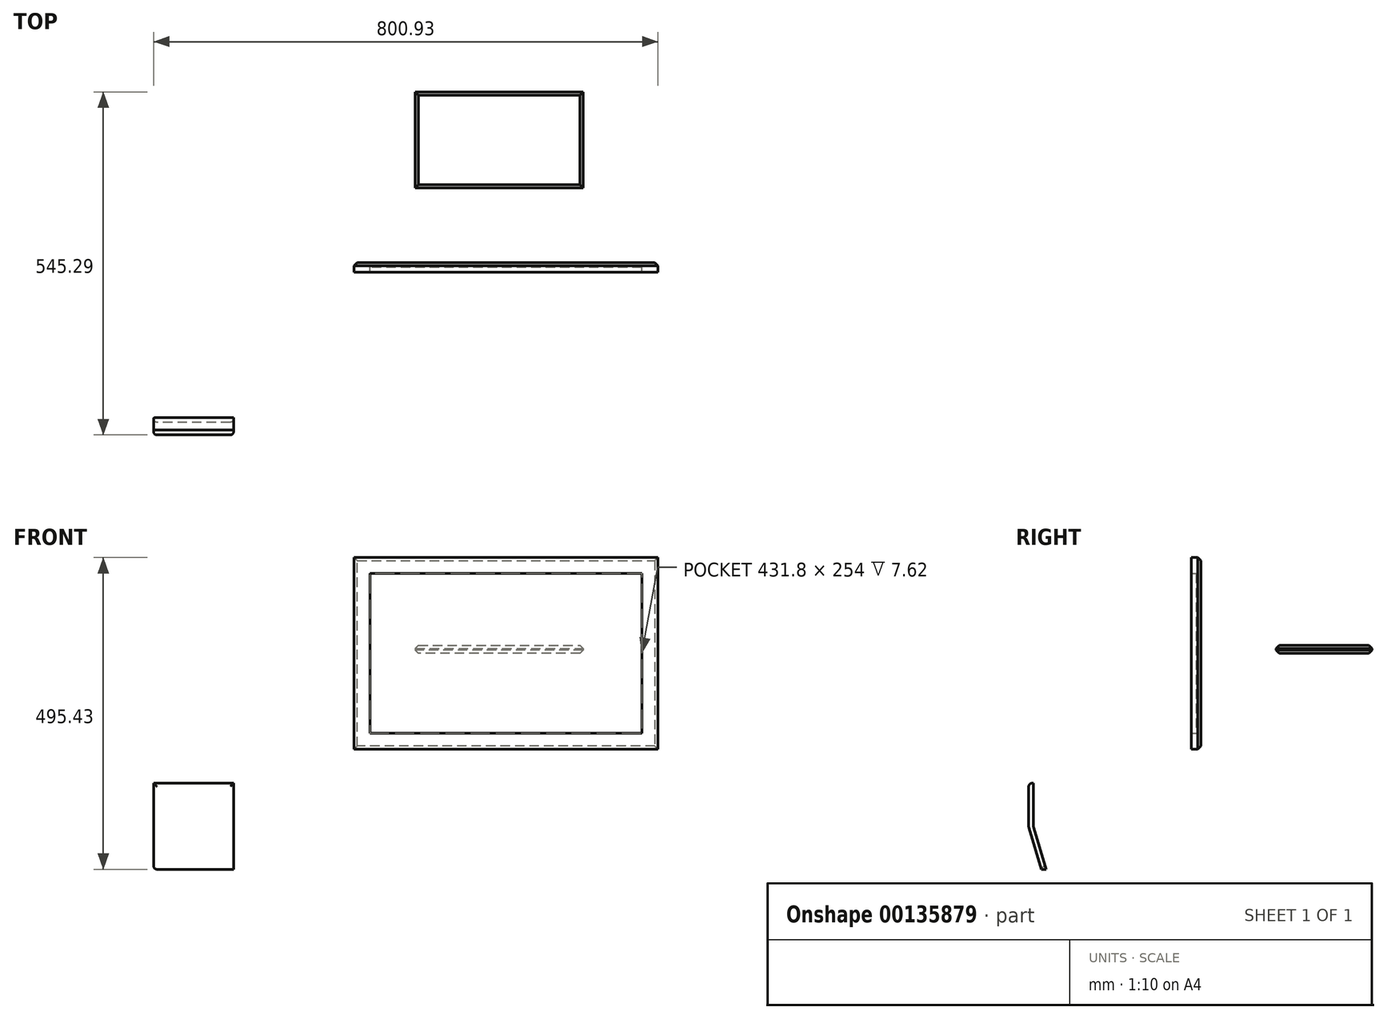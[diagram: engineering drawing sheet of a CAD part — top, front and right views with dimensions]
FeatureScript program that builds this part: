
annotation { "Feature Type Name" : "Feature", "Feature Type Description" : "" }
export const myFeature = defineFeature(function(context is Context, id is Id, definition is map)
    precondition{}
    {
        {
            var Q0;
            Q0=qCreatedBy(makeId("Front.planeOp"),FACE);
            var sketch = newSketch(context, id + "F0", { "sketchPlane" : qUnion([Q0])});
            skLineSegment(sketch, "E0.bottom", {"start": v(775.53, 127) * mm, "end": v(343.73, 127) * mm});
            skLineSegment(sketch, "E0.top", {"start": v(775.53, -127) * mm, "end": v(343.73, -127) * mm});
            skLineSegment(sketch, "E0.left", {"start": v(775.53, 127) * mm, "end": v(775.53, -127) * mm});
            skLineSegment(sketch, "E0.right", {"start": v(343.73, 127) * mm, "end": v(343.73, -127) * mm});
            skPoint(sketch, "E0.middle", {"position": v(559.63, 0) * mm});
            skLineSegment(sketch, "E1.bottom", {"start": v(800.93, -152.4) * mm, "end": v(318.33, -152.4) * mm});
            skLineSegment(sketch, "E1.top", {"start": v(800.93, 152.4) * mm, "end": v(318.33, 152.4) * mm});
            skLineSegment(sketch, "E1.left", {"start": v(800.93, -152.4) * mm, "end": v(800.93, 152.4) * mm});
            skLineSegment(sketch, "E1.right", {"start": v(318.33, -152.4) * mm, "end": v(318.33, 152.4) * mm});
            skPoint(sketch, "E2.middle", {"position": v(559.63, -218.6) * mm});
            skPoint(sketch, "E2.middle.positionSnap0", {"position": v(559.63, -152.4) * mm});
            skSolve(sketch);
        }
        {
            var Q0;
            Q0=makeQuery(id+"F0.imprint","IMPRINT",FACE,{"disambiguationData":[TD([[makeQuery(id+"F0.imprint","IMPRINT",EDGE,{"derivedFrom":sQuery(id+"F0.wireOp",EDGE,"E0.bottom")}),-1.0]])]});
            extrude(context, id + "F1", {"entities" : qUnion([Q0]), "depth" : 15.24 * mm});
        }
        {
            var Q0;
            Q0=makeQuery(id+"F0.imprint","IMPRINT",FACE,{"disambiguationData":[TD([[makeQuery(id+"F0.imprint","IMPRINT",EDGE,{"derivedFrom":sQuery(id+"F0.wireOp",EDGE,"E0.bottom")}),1.0]])]});
            extrude(context, id + "F2", {"entities" : qUnion([Q0]), "operationType" : NewBodyOperationType.ADD, "depth" : 7.62 * mm});
        }
        {
            var Q0;
            Q0=qCreatedBy(makeId("Top.planeOp"),FACE);
            var sketch = newSketch(context, id + "F3", { "sketchPlane" : qUnion([Q0])});
            skLineSegment(sketch, "E3.bottom", {"start": v(415.49, 271.65) * mm, "end": v(682.19, 271.65) * mm});
            skLineSegment(sketch, "E3.top", {"start": v(415.49, 119.25) * mm, "end": v(682.19, 119.25) * mm});
            skLineSegment(sketch, "E3.left", {"start": v(415.49, 271.65) * mm, "end": v(415.49, 119.25) * mm});
            skLineSegment(sketch, "E3.right", {"start": v(682.19, 271.65) * mm, "end": v(682.19, 119.25) * mm});
            skPoint(sketch, "E3.middle", {"position": v(548.84, 195.45) * mm});
            skSolve(sketch);
        }
        {
            var Q0;
            Q0=makeQuery(id+"F3.imprint","IMPRINT",FACE,{"disambiguationData":[TD([[makeQuery(id+"F3.imprint","IMPRINT",EDGE,{"derivedFrom":sQuery(id+"F3.wireOp",EDGE,"E3.bottom")}),-1.0]])]});
            extrude(context, id + "F4", {"entities" : qUnion([Q0]), "depth" : 12.7 * mm});
        }
        {
            var Q0;
            Q0=makeQuery(id+"F4.opExtrude","CAP_EDGE",EDGE,{"disambiguationData":[OSD([sQuery(id+"F3.wireOp",EDGE,"E3.bottom")])],"isStart":true});
            var Q1;
            Q1=makeQuery(id+"F4.opExtrude","CAP_EDGE",EDGE,{"disambiguationData":[OSD([sQuery(id+"F3.wireOp",EDGE,"E3.bottom")])],"isStart":false});
            var Q2;
            {var subQ0=sQuery(id+"F0.wireOp",EDGE,"E0.right");var subQ1=sQuery(id+"F0.wireOp",EDGE,"E0.left");var subQ2=sQuery(id+"F0.wireOp",EDGE,"E0.top");var subQ3=sQuery(id+"F0.wireOp",EDGE,"E0.bottom");Q2=makeQuery(id+"F2.boolean.opBoolean","MERGE",FACE,{"derivedFrom":[makeQuery(id+"F1.opExtrude","CAP_FACE",FACE,{"disambiguationData":[OSD([subQ3,subQ2,subQ1,subQ0,sQuery(id+"F0.wireOp",EDGE,"E1.bottom"),sQuery(id+"F0.wireOp",EDGE,"E1.top"),sQuery(id+"F0.wireOp",EDGE,"E1.left"),sQuery(id+"F0.wireOp",EDGE,"E1.right")])],"isStart":true}),makeQuery(id+"F2.opExtrude","CAP_FACE",FACE,{"disambiguationData":[OSD([subQ3,subQ2,subQ1,subQ0])],"isStart":true})]});}
            var Q3;
            Q3=makeQuery(id+"F4.opExtrude","CAP_EDGE",EDGE,{"disambiguationData":[OSD([sQuery(id+"F3.wireOp",EDGE,"E3.left")])],"isStart":true});
            var Q4;
            Q4=makeQuery(id+"F4.opExtrude","CAP_EDGE",EDGE,{"disambiguationData":[OSD([sQuery(id+"F3.wireOp",EDGE,"E3.left")])],"isStart":false});
            var Q5;
            Q5=makeQuery(id+"F4.opExtrude","CAP_EDGE",EDGE,{"disambiguationData":[OSD([sQuery(id+"F3.wireOp",EDGE,"E3.right")])],"isStart":true});
            var Q6;
            Q6=makeQuery(id+"F4.opExtrude","CAP_EDGE",EDGE,{"disambiguationData":[OSD([sQuery(id+"F3.wireOp",EDGE,"E3.right")])],"isStart":false});
            var Q7;
            Q7=makeQuery(id+"F4.opExtrude","CAP_EDGE",EDGE,{"disambiguationData":[OSD([sQuery(id+"F3.wireOp",EDGE,"E3.top")])],"isStart":false});
            var Q8;
            Q8=makeQuery(id+"F4.opExtrude","CAP_EDGE",EDGE,{"disambiguationData":[OSD([sQuery(id+"F3.wireOp",EDGE,"E3.top")])],"isStart":true});
            chamfer(context, id + "F5", {"entities" : qUnion([Q0, Q1, Q2, Q3, Q4, Q5, Q6, Q7, Q8]), "width" : 5.08 * mm, "tangentPropagation" : true});
        }
        {
            var Q0;
            Q0=qCreatedBy(makeId("Right.planeOp"),FACE);
            var sketch = newSketch(context, id + "F6", { "sketchPlane" : qUnion([Q0])});
            skLineSegment(sketch, "E4.bottom", {"start": v(-266.02, -206.3) * mm, "end": v(-273.64, -206.3) * mm});
            skLineSegment(sketch, "E4.top", {"start": v(-266.02, -276.15) * mm, "end": v(-273.64, -276.15) * mm});
            skLineSegment(sketch, "E4.left", {"start": v(-266.02, -206.3) * mm, "end": v(-266.02, -275.22) * mm});
            skLineSegment(sketch, "E4.right", {"start": v(-273.64, -206.3) * mm, "end": v(-273.64, -275.22) * mm});
            skLineSegment(sketch, "E5", {"start": v(-265.75, -277.05) * mm, "end": v(-245.86, -343.03) * mm});
            skLineSegment(sketch, "E6", {"start": v(-245.86, -343.03) * mm, "end": v(-253.48, -343.03) * mm});
            skLineSegment(sketch, "E7", {"start": v(-253.48, -343.03) * mm, "end": v(-273.37, -277.05) * mm});
            skPoint(sketch, "E8.visualSharp", {"position": v(-273.64, -276.15) * mm});
            skArc(sketch, "E8.filletArc", {"start": v(-273.64, -275.22) * mm, "mid": v(-273.57, -276.14) * mm, "end": v(-273.37, -277.05) * mm});
            skPoint(sketch, "E9.visualSharp", {"position": v(-266.02, -276.15) * mm});
            skArc(sketch, "E9.filletArc", {"start": v(-266.02, -275.22) * mm, "mid": v(-265.95, -276.14) * mm, "end": v(-265.75, -277.05) * mm});
            skSolve(sketch);
        }
        {
            var Q0;
            Q0 = qSketchRegion(id + "F6", true);
            extrude(context, id + "F7", {"entities" : qUnion([Q0]), "depth" : 127 * mm});
        }
        {
            var Q0;
            Q0=makeQuery(id+"F7.opExtrude","CAP_EDGE",EDGE,{"disambiguationData":[OSD([sQuery(id+"F6.wireOp",EDGE,"E6")])],"isStart":true});
            var Q1;
            Q1=makeQuery(id+"F7.opExtrude","CAP_EDGE",EDGE,{"disambiguationData":[OSD([sQuery(id+"F6.wireOp",EDGE,"E7")])],"isStart":true});
            var Q2;
            Q2=makeQuery(id+"F7.opExtrude","CAP_EDGE",EDGE,{"disambiguationData":[OSD([sQuery(id+"F6.wireOp",EDGE,"E4.right")])],"isStart":false});
            var Q3;
            Q3=makeQuery(id+"F7.opExtrude","SWEPT_EDGE",EDGE,{"disambiguationData":[OSD([sQuery(id+"F6.wireOp",EDGE,"E4.bottom"),sQuery(id+"F6.wireOp",EDGE,"E4.right")])]});
            var Q4;
            Q4=makeQuery(id+"F7.opExtrude","SWEPT_EDGE",EDGE,{"disambiguationData":[OSD([sQuery(id+"F6.wireOp",EDGE,"E4.right"),sQuery(id+"F6.wireOp",EDGE,"E8.filletArc")])]});
            fillet(context, id + "F8", {"entities" : qUnion([Q0, Q1, Q2, Q3, Q4]), "radius" : 5.08 * mm, "tangentPropagation" : true, "allowEdgeOverflow" : false});
        }
    });
